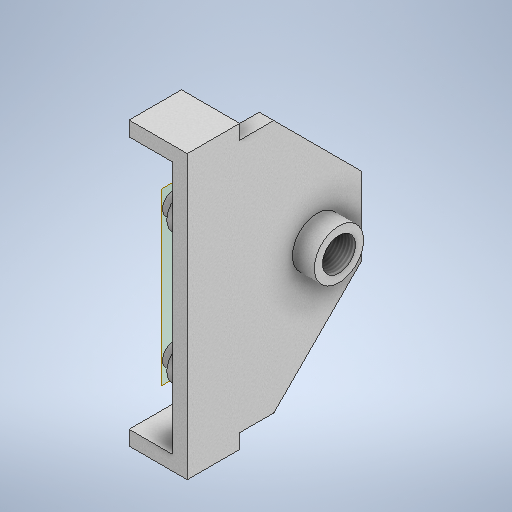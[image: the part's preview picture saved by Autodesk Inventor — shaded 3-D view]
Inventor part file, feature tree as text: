
AUTODESK INVENTOR PART (.ipt)
format: ipt  version: 2025.2 (Build 292293000, 293)  size: 391,680 bytes
history: native  units: in
note: dims shown in document units (in); Inventor stores cm internally (conversion verified against a paired STEP export)
features: extrude x7, other x4, thread x1, plane x1, hole x1, sketch x1
ambient origin geometry x8: Origin, YZ Plane, XZ Plane, XY Plane, X Axis, Y Axis, Z Axis, Center Point
bodies: Volumenkörper1 (feature_tree)
feature tree (15):
  other  "Skelett_Laufkatze.ipt"
  extrude  "Grundplatte"  Depth=0.3937in TaperAngle=0.0deg
  extrude  "Schutzwände"  Depth=0.3937in TaperAngle=0.0deg
  extrude  "Laufradaufhängung_1"  Depth=0.3937in TaperAngle=0.0deg
  extrude  "Laufradaufhängung_2"  Depth=0.3937in TaperAngle=0.0deg
  extrude  "Laufradaufhängung_3"  Depth=0.3937in TaperAngle=0.0deg
  extrude  "Laufradaufhängung_4"  Depth=0.3937in TaperAngle=0.0deg
  extrude  "Schraubbolzenöffnung"  Depth=0.3937in TaperAngle=0.0deg
  thread  "Gewinde1"  [1 undecoded]
  plane  "Arbeitsebene2"
  hole  "Bohrung1"  [1 undecoded]
  other  "Fuehrungsplatte_seite_ohne"
  other  "Fuehrungsplatte_Laufradaufhängung_ohne"
  other  "Fuehrungsplatte_Schraubbolzen_ohne"
  sketch  "Skizze5"  dims[d0=0.3937in d1=0.3937in d2=0.0in d3=0.3937in d4=0.0in d5=0.3937in d6=0.0in d7=0.3937in d8=0.0in d9=0.3937in d10=0.0in d11=0.3937in d12=0.0in d13=0.3937in d14=0.0in d15=1.9685in d16=0.0in d17=0.0in d18=0.3979in d19=0.9449in d20=0.1575in d21=0.0787in d22=90.0deg d23=1.2717in d24=0.8108in]
note: 2 required parameter values undecoded (feature->parameter linkage not recoverable at this tier; creation-order binding heuristic only, values carry confidence <= 0.55)
